# Revit family: Emergency_Equipment-Haws_Corporation-Eye_Wash_7261-7271
name_source: partatom
category: Plumbing Fixtures
revit_build: Autodesk Revit 2015 (Build: 20140606_1530(x64)
units: mm (PartAtom-declared; Revit-internal decimal feet)

## types (1)
- 7261-7271 - MSR Pedestal Mount Eye Face Wash
    Assembly Code = D2010610
    BIMobject category = Other
    Bowl Diameter = 0' - 11 1/4"
    Brand url = https://www.hawsco.com
    CW Connection = Yes
    Depth = 0' - 11 1/4"
    Description = MSR Pedestal Mount Eye/Face Wash
    Edition number = 1
    Finish = Metal - Haws Corporation - High Polished Stainless Steel
    Flow = 4 GPM
    HW Connection = No
    Height = 3' - 2"
    Installation instructions = https://www.hawsco.com
    Keynote = S12
    Manufacturer = Haws Corporation
    Manufacturer name = Haws Corporation
    Masterformat 2014 Code = 22 45 26
    Masterformat 2014 Description = Eye/Face Wash Equipment
    Model = 7261-7271
    Nominal height = 0' - 0"
    Nominal width = 0' - 0"
    OmniClass Code = 23-29 37 13 15
    OmniClass Description = Combination Emergency Eye Wash Stations
    Product Documentation Link = https://www.hawsco.com
    Product Guid = 2a6c366a-0d4b-4d15-93b3-e02926da890f
    Product Page URL = https://www.hawsco.com
    Product SKU = haws-7261-7271
    Product certification = https://www.hawsco.com
    Product data url = https://bimobject.com
    Product family = Eye Wash Fountains
    Product group = Emergency Equipment - Eye & Face Washes
    Product url = https://www.hawsco.com
    QR code = http://bimobject.com
    Sanitary Diameter = 0' - 1 1/4"
    Shower = Metal - Haws Corporation - Green Powder Coating
    Supply Diameter = 0' - 0 1/2"
    Technical description = https://www.hawsco.com
    UNSPSC Code = 46182402
    URL = https://www.hawsco.com
    Vent Connection = No
    Version = 2015 - v1.0a
    Warranty URL = https://www.hawsco.com
    Waste Connection = Yes
    Weight Net (Kg) = 0
    Width = 1' - 3"

## geometry (parser evidence)
native form markers: Sweep x2
no freeform markers — native parametric forms only
